# Revit family: Indoor_Pendant Lamp_Santa&Cole_Cirio Cascada
name_source: partatom
category: Luminarias
revit_build: Autodesk Revit 2018 (Build: 20190510_1515(x64)
units: mm (PartAtom-declared; Revit-internal decimal feet)

## family parameters
Anfitrión = Cara
Compartido = No
Corte con vacíos al cargar = No
Cota de conector redondo = Diámetro de uso
Origen de luz = No
Punto de cálculo de habitación = No
Tipo de pieza = Normal

## types (4) — shared parameters
Assembly Instructions - CE = https://www.santacole.com
Assembly Instructions - UL = https://www.santacole.com
Code = CIFxx+HEL0x+CIP0x
Elevación por defecto = 1219 mm
Energy Label = https://www.santacole.com
Fabricante = Santa & Cole
Manufacturer website = http://www.santacole.com
Modelo = Cirio Cascada
Technical Information = https://www.santacole.com
URL = https://www.santacole.com

## per-type parameters (varying)
| type | Carga aparente | Cirio Cascada 12 | Cirio Cascada 5 | Cirio Cascada 7 | Cirio Cascada 9 |
| Cirio Cascada 5 | 46 W | No | Sí | No | No |
| Cirio Cascada 7 | 65 W | No | No | Sí | No |
| Cirio Cascada 9 | 83 W | No | No | No | Sí |
| Cirio Cascada 12 | 0 W | Sí | No | No | No |

## geometry (parser evidence)
native form markers: Blend x2, Sweep x8
no freeform markers — native parametric forms only
